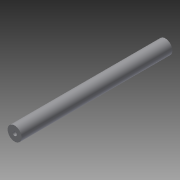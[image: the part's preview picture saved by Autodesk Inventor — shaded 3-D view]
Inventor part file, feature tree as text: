
AUTODESK INVENTOR PART (.ipt)
format: ipt  version: 2014 SP1 (Build 180222100, 222)  size: 74,752 bytes
history: native  units: in
note: dims shown in document units (in); Inventor stores cm internally (conversion verified against a paired STEP export)
features: extrude x1, sketch x1
ambient origin geometry x8: Origin, YZ Plane, XZ Plane, XY Plane, X Axis, Y Axis, Z Axis, Center Point
bodies: Solid1 (feature_tree)
feature tree (2):
  extrude  "Extrusion1"  Depth=26.875in
  sketch  "Sketch1"  dims[d0=2.5in d1=0.75in d2=26.875in d3=0.0in]
